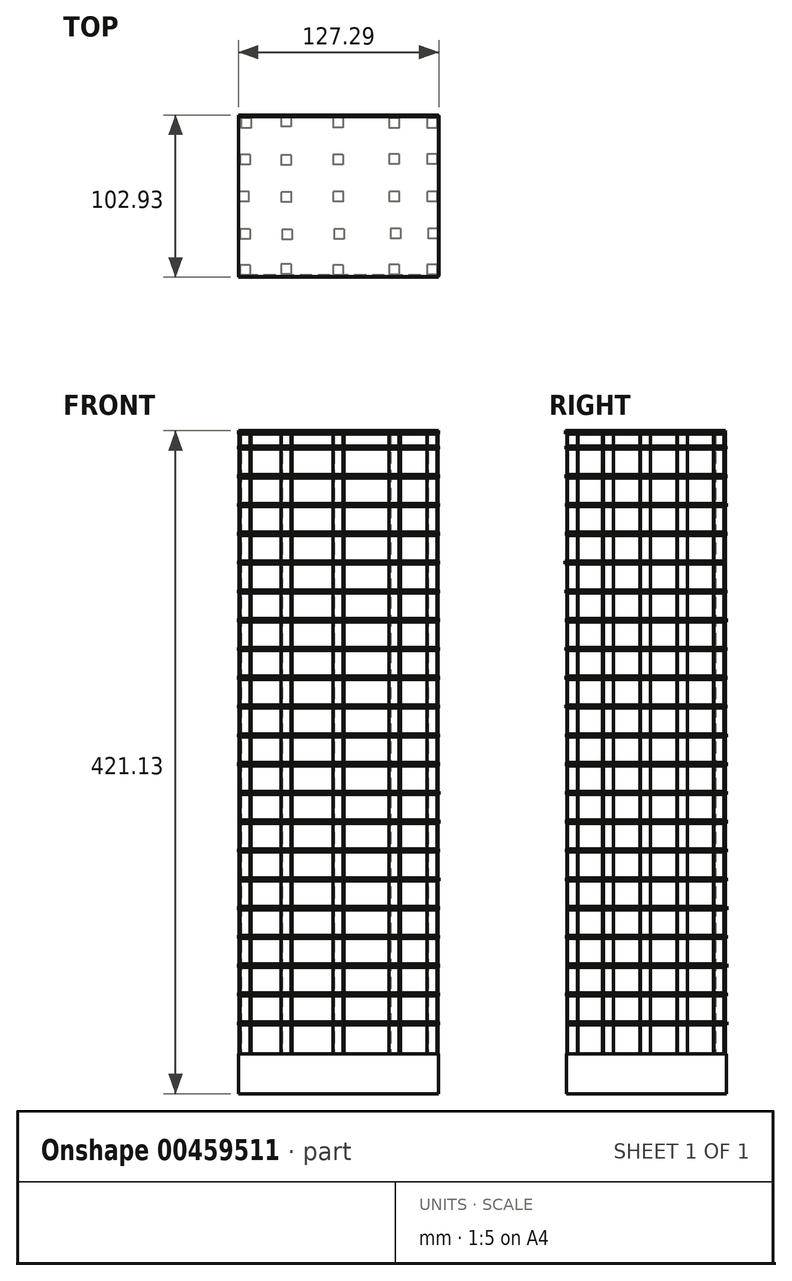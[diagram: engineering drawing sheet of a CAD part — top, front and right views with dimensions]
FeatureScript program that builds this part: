
annotation { "Feature Type Name" : "Feature", "Feature Type Description" : "" }
export const myFeature = defineFeature(function(context is Context, id is Id, definition is map)
    precondition{}
    {
        {
            var Q0;
            Q0=qCreatedBy(makeId("Top.planeOp"),FACE);
            var sketch = newSketch(context, id + "F0", { "sketchPlane" : qUnion([Q0])});
            skLineSegment(sketch, "E0.bottom", {"start": v(63.5, -50.8) * mm, "end": v(-63.5, -50.8) * mm});
            skLineSegment(sketch, "E0.top", {"start": v(63.5, 50.8) * mm, "end": v(-63.5, 50.8) * mm});
            skLineSegment(sketch, "E0.left", {"start": v(63.5, -50.8) * mm, "end": v(63.5, 50.8) * mm});
            skLineSegment(sketch, "E0.right", {"start": v(-63.5, -50.8) * mm, "end": v(-63.5, 50.8) * mm});
            skPoint(sketch, "E0.middle", {"position": v(0, 0) * mm});
            skSolve(sketch);
        }
        {
            var Q0;
            Q0 = qSketchRegion(id + "F0", true);
            extrude(context, id + "F1", {"entities" : qUnion([Q0]), "depth" : 2.03 * mm});
        }
        {
            var Q0;
            Q0=qCreatedBy(makeId("Top.planeOp"),FACE);
            var sketch = newSketch(context, id + "F2", { "sketchPlane" : qUnion([Q0])});
            skLineSegment(sketch, "E1.bottom", {"start": v(63.5, -51.15) * mm, "end": v(-63.5, -51.15) * mm});
            skLineSegment(sketch, "E1.top", {"start": v(63.5, 50.45) * mm, "end": v(-63.5, 50.45) * mm});
            skLineSegment(sketch, "E1.left", {"start": v(63.5, -51.15) * mm, "end": v(63.5, 50.45) * mm});
            skLineSegment(sketch, "E1.right", {"start": v(-63.5, -51.15) * mm, "end": v(-63.5, 50.45) * mm});
            skPoint(sketch, "E1.middle", {"position": v(0, -0.35) * mm});
            skSolve(sketch);
        }
        {
            var Q0;
            Q0=makeQuery(id+"F1.opExtrude","SWEPT_BODY",BODY,{"disambiguationData":[OSD([sQuery(id+"F0.wireOp",EDGE,"E0.bottom"),sQuery(id+"F0.wireOp",EDGE,"E0.top"),sQuery(id+"F0.wireOp",EDGE,"E0.left"),sQuery(id+"F0.wireOp",EDGE,"E0.right")])]});
            transform(context, id + "F3", {"entities" : qUnion([Q0]), "transformType" : TransformType.TRANSLATION_3D, "dx" : 0 * mm, "dy" : 0 * mm, "dz" : 18.29 * mm, "makeCopy" : false});
        }
        {
            var Q0;
            Q0 = qSketchRegion(id + "F2", true);
            extrude(context, id + "F4", {"entities" : qUnion([Q0]), "depth" : 2.03 * mm});
        }
        {
            var Q0;
            Q0=qCreatedBy(makeId("Top.planeOp"),FACE);
            var sketch = newSketch(context, id + "F5", { "sketchPlane" : qUnion([Q0])});
            skLineSegment(sketch, "E2.bottom", {"start": v(63.5, -50.92) * mm, "end": v(-63.5, -50.92) * mm});
            skLineSegment(sketch, "E2.top", {"start": v(63.5, 50.68) * mm, "end": v(-63.5, 50.68) * mm});
            skLineSegment(sketch, "E2.left", {"start": v(63.5, -50.92) * mm, "end": v(63.5, 50.68) * mm});
            skLineSegment(sketch, "E2.right", {"start": v(-63.5, -50.92) * mm, "end": v(-63.5, 50.68) * mm});
            skPoint(sketch, "E2.middle", {"position": v(0, -0.12) * mm});
            skSolve(sketch);
        }
        {
            var Q0;
            Q0=makeQuery(id+"F4.opExtrude","SWEPT_BODY",BODY,{"disambiguationData":[OSD([sQuery(id+"F2.wireOp",EDGE,"E1.bottom"),sQuery(id+"F2.wireOp",EDGE,"E1.top"),sQuery(id+"F2.wireOp",EDGE,"E1.left"),sQuery(id+"F2.wireOp",EDGE,"E1.right")])]});
            transform(context, id + "F6", {"entities" : qUnion([Q0]), "transformType" : TransformType.TRANSLATION_3D, "dx" : 0 * mm, "dy" : 0 * mm, "dz" : 36.58 * mm, "makeCopy" : false});
        }
        {
            var Q0;
            Q0 = qSketchRegion(id + "F5", true);
            extrude(context, id + "F7", {"entities" : qUnion([Q0]), "depth" : 2.03 * mm});
        }
        {
            var Q0;
            Q0=qCreatedBy(makeId("Top.planeOp"),FACE);
            var sketch = newSketch(context, id + "F8", { "sketchPlane" : qUnion([Q0])});
            skLineSegment(sketch, "E3.bottom", {"start": v(63.5, -51.15) * mm, "end": v(-63.5, -51.15) * mm});
            skLineSegment(sketch, "E3.top", {"start": v(63.5, 50.45) * mm, "end": v(-63.5, 50.45) * mm});
            skLineSegment(sketch, "E3.left", {"start": v(63.5, -51.15) * mm, "end": v(63.5, 50.45) * mm});
            skLineSegment(sketch, "E3.right", {"start": v(-63.5, -51.15) * mm, "end": v(-63.5, 50.45) * mm});
            skPoint(sketch, "E3.middle", {"position": v(0, -0.35) * mm});
            skSolve(sketch);
        }
        {
            var Q0;
            Q0=makeQuery(id+"F7.opExtrude","SWEPT_BODY",BODY,{"disambiguationData":[OSD([sQuery(id+"F5.wireOp",EDGE,"E2.bottom"),sQuery(id+"F5.wireOp",EDGE,"E2.top"),sQuery(id+"F5.wireOp",EDGE,"E2.left"),sQuery(id+"F5.wireOp",EDGE,"E2.right")])]});
            transform(context, id + "F9", {"entities" : qUnion([Q0]), "transformType" : TransformType.TRANSLATION_3D, "dx" : 0 * mm, "dy" : 0 * mm, "dz" : 54.86 * mm, "makeCopy" : false});
        }
        {
            var Q0;
            Q0 = qSketchRegion(id + "F8", true);
            var Q1;
            Q1=qNothing();
            extrude(context, id + "F10", {"entities" : qUnion([Q0, Q1]), "operationType" : NewBodyOperationType.ADD, "depth" : 2.03 * mm});
        }
        {
            var Q0;
            Q0=qCreatedBy(makeId("Top.planeOp"),FACE);
            var sketch = newSketch(context, id + "F11", { "sketchPlane" : qUnion([Q0])});
            skLineSegment(sketch, "E4.bottom", {"start": v(63.5, -50.92) * mm, "end": v(-63.5, -50.92) * mm});
            skLineSegment(sketch, "E4.top", {"start": v(63.5, 50.68) * mm, "end": v(-63.5, 50.68) * mm});
            skLineSegment(sketch, "E4.left", {"start": v(63.5, -50.92) * mm, "end": v(63.5, 50.68) * mm});
            skLineSegment(sketch, "E4.right", {"start": v(-63.5, -50.92) * mm, "end": v(-63.5, 50.68) * mm});
            skPoint(sketch, "E4.middle", {"position": v(0, -0.12) * mm});
            skSolve(sketch);
        }
        {
            var Q0;
            Q0=makeQuery(id+"F10.opExtrude","SWEPT_BODY",BODY,{"disambiguationData":[OSD([sQuery(id+"F8.wireOp",EDGE,"E3.bottom"),sQuery(id+"F8.wireOp",EDGE,"E3.top"),sQuery(id+"F8.wireOp",EDGE,"E3.left"),sQuery(id+"F8.wireOp",EDGE,"E3.right")])]});
            transform(context, id + "F12", {"entities" : qUnion([Q0]), "transformType" : TransformType.TRANSLATION_3D, "dx" : 0 * mm, "dy" : 0 * mm, "dz" : 73.15 * mm, "makeCopy" : false});
        }
        {
            var Q0;
            Q0 = qSketchRegion(id + "F11", true);
            extrude(context, id + "F13", {"entities" : qUnion([Q0]), "depth" : 2.03 * mm});
        }
        {
            var Q0;
            Q0=qCreatedBy(makeId("Top.planeOp"),FACE);
            var sketch = newSketch(context, id + "F14", { "sketchPlane" : qUnion([Q0])});
            skLineSegment(sketch, "E5.bottom", {"start": v(63.75, -51.12) * mm, "end": v(-63.25, -51.12) * mm});
            skLineSegment(sketch, "E5.top", {"start": v(63.75, 50.48) * mm, "end": v(-63.25, 50.48) * mm});
            skLineSegment(sketch, "E5.left", {"start": v(63.75, -51.12) * mm, "end": v(63.75, 50.48) * mm});
            skLineSegment(sketch, "E5.right", {"start": v(-63.25, -51.12) * mm, "end": v(-63.25, 50.48) * mm});
            skPoint(sketch, "E5.middle", {"position": v(0.25, -0.32) * mm});
            skSolve(sketch);
        }
        {
            var Q0;
            Q0=makeQuery(id+"F13.opExtrude","SWEPT_BODY",BODY,{"disambiguationData":[OSD([sQuery(id+"F11.wireOp",EDGE,"E4.bottom"),sQuery(id+"F11.wireOp",EDGE,"E4.top"),sQuery(id+"F11.wireOp",EDGE,"E4.left"),sQuery(id+"F11.wireOp",EDGE,"E4.right")])]});
            transform(context, id + "F15", {"entities" : qUnion([Q0]), "transformType" : TransformType.TRANSLATION_3D, "dx" : 0 * mm, "dy" : 0 * mm, "dz" : 91.44 * mm, "makeCopy" : false});
        }
        {
            var Q0;
            Q0 = qSketchRegion(id + "F14", true);
            extrude(context, id + "F16", {"entities" : qUnion([Q0]), "depth" : 2.03 * mm});
        }
        {
            var Q0;
            Q0=qCreatedBy(makeId("Top.planeOp"),FACE);
            var sketch = newSketch(context, id + "F17", { "sketchPlane" : qUnion([Q0])});
            skLineSegment(sketch, "E6.bottom", {"start": v(63.56, -50.99) * mm, "end": v(-63.44, -50.99) * mm});
            skLineSegment(sketch, "E6.top", {"start": v(63.56, 50.61) * mm, "end": v(-63.44, 50.61) * mm});
            skLineSegment(sketch, "E6.left", {"start": v(63.56, -50.99) * mm, "end": v(63.56, 50.61) * mm});
            skLineSegment(sketch, "E6.right", {"start": v(-63.44, -50.99) * mm, "end": v(-63.44, 50.61) * mm});
            skPoint(sketch, "E6.middle", {"position": v(0.06, -0.19) * mm});
            skSolve(sketch);
        }
        {
            var Q0;
            Q0=makeQuery(id+"F16.opExtrude","SWEPT_BODY",BODY,{"disambiguationData":[OSD([sQuery(id+"F14.wireOp",EDGE,"E5.bottom"),sQuery(id+"F14.wireOp",EDGE,"E5.top"),sQuery(id+"F14.wireOp",EDGE,"E5.left"),sQuery(id+"F14.wireOp",EDGE,"E5.right")])]});
            transform(context, id + "F18", {"entities" : qUnion([Q0]), "transformType" : TransformType.TRANSLATION_3D, "dx" : 0 * mm, "dy" : 0 * mm, "dz" : 109.73 * mm, "makeCopy" : false});
        }
        {
            var Q0;
            Q0 = qSketchRegion(id + "F17", true);
            extrude(context, id + "F19", {"entities" : qUnion([Q0]), "depth" : 2.03 * mm});
        }
        {
            var Q0;
            Q0=qCreatedBy(makeId("Top.planeOp"),FACE);
            var sketch = newSketch(context, id + "F20", { "sketchPlane" : qUnion([Q0])});
            skLineSegment(sketch, "E7.bottom", {"start": v(63.79, -51.09) * mm, "end": v(-63.21, -51.09) * mm});
            skLineSegment(sketch, "E7.top", {"start": v(63.79, 50.51) * mm, "end": v(-63.21, 50.51) * mm});
            skLineSegment(sketch, "E7.left", {"start": v(63.79, -51.09) * mm, "end": v(63.79, 50.51) * mm});
            skLineSegment(sketch, "E7.right", {"start": v(-63.21, -51.09) * mm, "end": v(-63.21, 50.51) * mm});
            skSolve(sketch);
        }
        {
            var Q0;
            Q0=makeQuery(id+"F19.opExtrude","SWEPT_BODY",BODY,{"disambiguationData":[OSD([sQuery(id+"F17.wireOp",EDGE,"E6.bottom"),sQuery(id+"F17.wireOp",EDGE,"E6.top"),sQuery(id+"F17.wireOp",EDGE,"E6.left"),sQuery(id+"F17.wireOp",EDGE,"E6.right")])]});
            transform(context, id + "F21", {"entities" : qUnion([Q0]), "transformType" : TransformType.TRANSLATION_3D, "dx" : 0 * mm, "dy" : 0 * mm, "dz" : 128.02 * mm, "makeCopy" : false});
        }
        {
            var Q0;
            Q0 = qSketchRegion(id + "F20", true);
            extrude(context, id + "F22", {"entities" : qUnion([Q0]), "depth" : 2.03 * mm});
        }
        {
            var Q0;
            Q0=qCreatedBy(makeId("Top.planeOp"),FACE);
            var sketch = newSketch(context, id + "F23", { "sketchPlane" : qUnion([Q0])});
            skLineSegment(sketch, "E8.bottom", {"start": v(63.79, -51.09) * mm, "end": v(-63.21, -51.09) * mm});
            skLineSegment(sketch, "E8.top", {"start": v(63.79, 50.51) * mm, "end": v(-63.21, 50.51) * mm});
            skLineSegment(sketch, "E8.left", {"start": v(63.79, -51.09) * mm, "end": v(63.79, 50.51) * mm});
            skLineSegment(sketch, "E8.right", {"start": v(-63.21, -51.09) * mm, "end": v(-63.21, 50.51) * mm});
            skSolve(sketch);
        }
        {
            var Q0;
            Q0=makeQuery(id+"F22.opExtrude","SWEPT_BODY",BODY,{"disambiguationData":[OSD([sQuery(id+"F20.wireOp",EDGE,"E7.bottom"),sQuery(id+"F20.wireOp",EDGE,"E7.top"),sQuery(id+"F20.wireOp",EDGE,"E7.left"),sQuery(id+"F20.wireOp",EDGE,"E7.right")])]});
            transform(context, id + "F24", {"entities" : qUnion([Q0]), "transformType" : TransformType.TRANSLATION_3D, "dx" : 0 * mm, "dy" : 0 * mm, "dz" : 146.3 * mm, "makeCopy" : false});
        }
        {
            var Q0;
            Q0 = qSketchRegion(id + "F23", true);
            extrude(context, id + "F25", {"entities" : qUnion([Q0]), "depth" : 2.03 * mm});
        }
        {
            var Q0;
            Q0=qCreatedBy(makeId("Top.planeOp"),FACE);
            var sketch = newSketch(context, id + "F26", { "sketchPlane" : qUnion([Q0])});
            skLineSegment(sketch, "E9.bottom", {"start": v(63.5, -51.09) * mm, "end": v(-63.5, -51.09) * mm});
            skLineSegment(sketch, "E9.top", {"start": v(63.5, 50.51) * mm, "end": v(-63.5, 50.51) * mm});
            skLineSegment(sketch, "E9.left", {"start": v(63.5, -51.09) * mm, "end": v(63.5, 50.51) * mm});
            skLineSegment(sketch, "E9.right", {"start": v(-63.5, -51.09) * mm, "end": v(-63.5, 50.51) * mm});
            skSolve(sketch);
        }
        {
            var Q0;
            Q0=makeQuery(id+"F25.opExtrude","SWEPT_BODY",BODY,{"disambiguationData":[OSD([sQuery(id+"F23.wireOp",EDGE,"E8.bottom"),sQuery(id+"F23.wireOp",EDGE,"E8.top"),sQuery(id+"F23.wireOp",EDGE,"E8.left"),sQuery(id+"F23.wireOp",EDGE,"E8.right")])]});
            transform(context, id + "F27", {"entities" : qUnion([Q0]), "transformType" : TransformType.TRANSLATION_3D, "dx" : 0 * mm, "dy" : 0 * mm, "dz" : 164.6 * mm, "makeCopy" : false});
        }
        {
            var Q0;
            Q0 = qSketchRegion(id + "F26", true);
            extrude(context, id + "F28", {"entities" : qUnion([Q0]), "depth" : 2.03 * mm});
        }
        {
            var Q0;
            Q0=qCreatedBy(makeId("Top.planeOp"),FACE);
            var sketch = newSketch(context, id + "F29", { "sketchPlane" : qUnion([Q0])});
            skLineSegment(sketch, "E10.bottom", {"start": v(63.5, -51.09) * mm, "end": v(-63.5, -51.09) * mm});
            skLineSegment(sketch, "E10.top", {"start": v(63.5, 50.51) * mm, "end": v(-63.5, 50.51) * mm});
            skLineSegment(sketch, "E10.left", {"start": v(63.5, -51.09) * mm, "end": v(63.5, 50.51) * mm});
            skLineSegment(sketch, "E10.right", {"start": v(-63.5, -51.09) * mm, "end": v(-63.5, 50.51) * mm});
            skSolve(sketch);
        }
        {
            var Q0;
            Q0=makeQuery(id+"F28.opExtrude","SWEPT_BODY",BODY,{"disambiguationData":[OSD([sQuery(id+"F26.wireOp",EDGE,"E9.bottom"),sQuery(id+"F26.wireOp",EDGE,"E9.top"),sQuery(id+"F26.wireOp",EDGE,"E9.left"),sQuery(id+"F26.wireOp",EDGE,"E9.right")])]});
            transform(context, id + "F30", {"entities" : qUnion([Q0]), "transformType" : TransformType.TRANSLATION_3D, "dx" : 0 * mm, "dy" : 0 * mm, "dz" : 182.88 * mm, "makeCopy" : false});
        }
        {
            var Q0;
            Q0 = qSketchRegion(id + "F29", true);
            extrude(context, id + "F31", {"entities" : qUnion([Q0]), "depth" : 2.03 * mm});
        }
        {
            var Q0;
            Q0=qCreatedBy(makeId("Top.planeOp"),FACE);
            var sketch = newSketch(context, id + "F32", { "sketchPlane" : qUnion([Q0])});
            skLineSegment(sketch, "E11.bottom", {"start": v(63.5, -51.35) * mm, "end": v(-63.5, -51.35) * mm});
            skLineSegment(sketch, "E11.top", {"start": v(63.5, 50.25) * mm, "end": v(-63.5, 50.25) * mm});
            skLineSegment(sketch, "E11.left", {"start": v(63.5, -51.35) * mm, "end": v(63.5, 50.25) * mm});
            skLineSegment(sketch, "E11.right", {"start": v(-63.5, -51.35) * mm, "end": v(-63.5, 50.25) * mm});
            skSolve(sketch);
        }
        {
            var Q0;
            Q0=makeQuery(id+"F31.opExtrude","SWEPT_BODY",BODY,{"disambiguationData":[OSD([sQuery(id+"F29.wireOp",EDGE,"E10.bottom"),sQuery(id+"F29.wireOp",EDGE,"E10.top"),sQuery(id+"F29.wireOp",EDGE,"E10.left"),sQuery(id+"F29.wireOp",EDGE,"E10.right")])]});
            transform(context, id + "F33", {"entities" : qUnion([Q0]), "transformType" : TransformType.TRANSLATION_3D, "dx" : 0 * mm, "dy" : 0 * mm, "dz" : 201.17 * mm, "makeCopy" : false});
        }
        {
            var Q0;
            Q0 = qSketchRegion(id + "F32", true);
            extrude(context, id + "F34", {"entities" : qUnion([Q0]), "depth" : 2.03 * mm});
        }
        {
            var Q0;
            Q0=qCreatedBy(makeId("Top.planeOp"),FACE);
            var sketch = newSketch(context, id + "F35", { "sketchPlane" : qUnion([Q0])});
            skLineSegment(sketch, "E12.bottom", {"start": v(63.5, -51.42) * mm, "end": v(-63.5, -51.42) * mm});
            skLineSegment(sketch, "E12.top", {"start": v(63.5, 50.18) * mm, "end": v(-63.5, 50.18) * mm});
            skLineSegment(sketch, "E12.left", {"start": v(63.5, -51.42) * mm, "end": v(63.5, 50.18) * mm});
            skLineSegment(sketch, "E12.right", {"start": v(-63.5, -51.42) * mm, "end": v(-63.5, 50.18) * mm});
            skSolve(sketch);
        }
        {
            var Q0;
            Q0=makeQuery(id+"F34.opExtrude","SWEPT_BODY",BODY,{"disambiguationData":[OSD([sQuery(id+"F32.wireOp",EDGE,"E11.bottom"),sQuery(id+"F32.wireOp",EDGE,"E11.top"),sQuery(id+"F32.wireOp",EDGE,"E11.left"),sQuery(id+"F32.wireOp",EDGE,"E11.right")])]});
            transform(context, id + "F36", {"entities" : qUnion([Q0]), "transformType" : TransformType.TRANSLATION_3D, "dx" : 0 * mm, "dy" : 0 * mm, "dz" : 219.46 * mm, "makeCopy" : false});
        }
        {
            var Q0;
            Q0=makeQuery(id+"F35.imprint","IMPRINT",FACE,{"disambiguationData":[TD([[makeQuery(id+"F35.imprint","IMPRINT",EDGE,{"derivedFrom":sQuery(id+"F35.wireOp",EDGE,"E12.bottom")}),-1.0]])]});
            extrude(context, id + "F37", {"entities" : qUnion([Q0]), "depth" : 2.03 * mm});
        }
        {
            var Q0;
            Q0=qCreatedBy(makeId("Top.planeOp"),FACE);
            var sketch = newSketch(context, id + "F38", { "sketchPlane" : qUnion([Q0])});
            skLineSegment(sketch, "E13.bottom", {"start": v(63.5, -51.4) * mm, "end": v(-63.5, -51.4) * mm});
            skLineSegment(sketch, "E13.top", {"start": v(63.5, 50.2) * mm, "end": v(-63.5, 50.2) * mm});
            skLineSegment(sketch, "E13.left", {"start": v(63.5, -51.4) * mm, "end": v(63.5, 50.2) * mm});
            skLineSegment(sketch, "E13.right", {"start": v(-63.5, -51.4) * mm, "end": v(-63.5, 50.2) * mm});
            skSolve(sketch);
        }
        {
            var Q0;
            Q0=makeQuery(id+"F37.opExtrude","SWEPT_BODY",BODY,{"disambiguationData":[OSD([sQuery(id+"F35.wireOp",EDGE,"E12.bottom"),sQuery(id+"F35.wireOp",EDGE,"E12.top"),sQuery(id+"F35.wireOp",EDGE,"E12.left"),sQuery(id+"F35.wireOp",EDGE,"E12.right")])]});
            transform(context, id + "F39", {"entities" : qUnion([Q0]), "transformType" : TransformType.TRANSLATION_3D, "dx" : 0 * mm, "dy" : 0 * mm, "dz" : 237.74 * mm, "makeCopy" : false});
        }
        {
            var Q0;
            Q0=makeQuery(id+"F38.imprint","IMPRINT",FACE,{"disambiguationData":[TD([[makeQuery(id+"F38.imprint","IMPRINT",EDGE,{"derivedFrom":sQuery(id+"F38.wireOp",EDGE,"E13.bottom")}),-1.0]])]});
            extrude(context, id + "F40", {"entities" : qUnion([Q0]), "depth" : 2.03 * mm});
        }
        {
            var Q0;
            Q0=qCreatedBy(makeId("Top.planeOp"),FACE);
            var sketch = newSketch(context, id + "F41", { "sketchPlane" : qUnion([Q0])});
            skLineSegment(sketch, "E14.bottom", {"start": v(63.5, -51.26) * mm, "end": v(-63.5, -51.26) * mm});
            skLineSegment(sketch, "E14.top", {"start": v(63.5, 50.34) * mm, "end": v(-63.5, 50.34) * mm});
            skLineSegment(sketch, "E14.left", {"start": v(63.5, -51.26) * mm, "end": v(63.5, 50.34) * mm});
            skLineSegment(sketch, "E14.right", {"start": v(-63.5, -51.26) * mm, "end": v(-63.5, 50.34) * mm});
            skSolve(sketch);
        }
        {
            var Q0;
            Q0=makeQuery(id+"F40.opExtrude","SWEPT_BODY",BODY,{"disambiguationData":[OSD([sQuery(id+"F38.wireOp",EDGE,"E13.bottom"),sQuery(id+"F38.wireOp",EDGE,"E13.top"),sQuery(id+"F38.wireOp",EDGE,"E13.left"),sQuery(id+"F38.wireOp",EDGE,"E13.right")])]});
            transform(context, id + "F42", {"entities" : qUnion([Q0]), "transformType" : TransformType.TRANSLATION_3D, "dx" : 0 * mm, "dy" : 0 * mm, "dz" : 256.03 * mm, "makeCopy" : false});
        }
        {
            var Q0;
            Q0=makeQuery(id+"F41.imprint","IMPRINT",FACE,{"disambiguationData":[TD([[makeQuery(id+"F41.imprint","IMPRINT",EDGE,{"derivedFrom":sQuery(id+"F41.wireOp",EDGE,"E14.bottom")}),-1.0]])]});
            extrude(context, id + "F43", {"entities" : qUnion([Q0]), "depth" : 2.03 * mm});
        }
        {
            var Q0;
            Q0=qCreatedBy(makeId("Top.planeOp"),FACE);
            var sketch = newSketch(context, id + "F44", { "sketchPlane" : qUnion([Q0])});
            skLineSegment(sketch, "E15.bottom", {"start": v(63.5, -51.43) * mm, "end": v(-63.5, -51.43) * mm});
            skLineSegment(sketch, "E15.top", {"start": v(63.5, 50.17) * mm, "end": v(-63.5, 50.17) * mm});
            skLineSegment(sketch, "E15.left", {"start": v(63.5, -51.43) * mm, "end": v(63.5, 50.17) * mm});
            skLineSegment(sketch, "E15.right", {"start": v(-63.5, -51.43) * mm, "end": v(-63.5, 50.17) * mm});
            skSolve(sketch);
        }
        {
            var Q0;
            Q0=makeQuery(id+"F43.opExtrude","SWEPT_BODY",BODY,{"disambiguationData":[OSD([sQuery(id+"F41.wireOp",EDGE,"E14.bottom"),sQuery(id+"F41.wireOp",EDGE,"E14.top"),sQuery(id+"F41.wireOp",EDGE,"E14.left"),sQuery(id+"F41.wireOp",EDGE,"E14.right")])]});
            transform(context, id + "F45", {"entities" : qUnion([Q0]), "transformType" : TransformType.TRANSLATION_3D, "dx" : 0 * mm, "dy" : 0 * mm, "dz" : 274.32 * mm, "makeCopy" : false});
        }
        {
            var Q0;
            Q0=makeQuery(id+"F44.imprint","IMPRINT",FACE,{"disambiguationData":[TD([[makeQuery(id+"F44.imprint","IMPRINT",EDGE,{"derivedFrom":sQuery(id+"F44.wireOp",EDGE,"E15.bottom")}),-1.0]])]});
            extrude(context, id + "F46", {"entities" : qUnion([Q0]), "depth" : 2.03 * mm});
        }
        {
            var Q0;
            Q0=qCreatedBy(makeId("Top.planeOp"),FACE);
            var sketch = newSketch(context, id + "F47", { "sketchPlane" : qUnion([Q0])});
            skLineSegment(sketch, "E16.bottom", {"start": v(63.5, -52.13) * mm, "end": v(-63.5, -52.13) * mm});
            skLineSegment(sketch, "E16.top", {"start": v(63.5, 49.47) * mm, "end": v(-63.5, 49.47) * mm});
            skLineSegment(sketch, "E16.left", {"start": v(63.5, -52.13) * mm, "end": v(63.5, 49.47) * mm});
            skLineSegment(sketch, "E16.right", {"start": v(-63.5, -52.13) * mm, "end": v(-63.5, 49.47) * mm});
            skSolve(sketch);
        }
        {
            var Q0;
            Q0=makeQuery(id+"F46.opExtrude","SWEPT_BODY",BODY,{"disambiguationData":[OSD([sQuery(id+"F44.wireOp",EDGE,"E15.bottom"),sQuery(id+"F44.wireOp",EDGE,"E15.top"),sQuery(id+"F44.wireOp",EDGE,"E15.left"),sQuery(id+"F44.wireOp",EDGE,"E15.right")])]});
            transform(context, id + "F48", {"entities" : qUnion([Q0]), "transformType" : TransformType.TRANSLATION_3D, "dx" : 0 * mm, "dy" : 0 * mm, "dz" : 292.6 * mm, "makeCopy" : false});
        }
        {
            var Q0;
            Q0=makeQuery(id+"F47.imprint","IMPRINT",FACE,{"disambiguationData":[TD([[makeQuery(id+"F47.imprint","IMPRINT",EDGE,{"derivedFrom":sQuery(id+"F47.wireOp",EDGE,"E16.bottom")}),-1.0]])]});
            extrude(context, id + "F49", {"entities" : qUnion([Q0]), "depth" : 2.03 * mm});
        }
        {
            var Q0;
            Q0=qCreatedBy(makeId("Top.planeOp"),FACE);
            var sketch = newSketch(context, id + "F50", { "sketchPlane" : qUnion([Q0])});
            skLineSegment(sketch, "E17.bottom", {"start": v(63.5, -51.27) * mm, "end": v(-63.5, -51.27) * mm});
            skLineSegment(sketch, "E17.top", {"start": v(63.5, 50.33) * mm, "end": v(-63.5, 50.33) * mm});
            skLineSegment(sketch, "E17.left", {"start": v(63.5, -51.27) * mm, "end": v(63.5, 50.33) * mm});
            skLineSegment(sketch, "E17.right", {"start": v(-63.5, -51.27) * mm, "end": v(-63.5, 50.33) * mm});
            skSolve(sketch);
        }
        {
            var Q0;
            Q0=makeQuery(id+"F49.opExtrude","SWEPT_BODY",BODY,{"disambiguationData":[OSD([sQuery(id+"F47.wireOp",EDGE,"E16.bottom"),sQuery(id+"F47.wireOp",EDGE,"E16.top"),sQuery(id+"F47.wireOp",EDGE,"E16.left"),sQuery(id+"F47.wireOp",EDGE,"E16.right")])]});
            transform(context, id + "F51", {"entities" : qUnion([Q0]), "transformType" : TransformType.TRANSLATION_3D, "dx" : 0 * mm, "dy" : 0 * mm, "dz" : 310.9 * mm, "makeCopy" : false});
        }
        {
            var Q0;
            Q0=makeQuery(id+"F50.imprint","IMPRINT",FACE,{"disambiguationData":[TD([[makeQuery(id+"F50.imprint","IMPRINT",EDGE,{"derivedFrom":sQuery(id+"F50.wireOp",EDGE,"E17.bottom")}),-1.0]])]});
            extrude(context, id + "F52", {"entities" : qUnion([Q0]), "depth" : 2.03 * mm});
        }
        {
            var Q0;
            Q0=qCreatedBy(makeId("Top.planeOp"),FACE);
            var sketch = newSketch(context, id + "F53", { "sketchPlane" : qUnion([Q0])});
            skLineSegment(sketch, "E18.bottom", {"start": v(63.5, -51.08) * mm, "end": v(-63.5, -51.08) * mm});
            skLineSegment(sketch, "E18.top", {"start": v(63.5, 50.52) * mm, "end": v(-63.5, 50.52) * mm});
            skLineSegment(sketch, "E18.left", {"start": v(63.5, -51.08) * mm, "end": v(63.5, 50.52) * mm});
            skLineSegment(sketch, "E18.right", {"start": v(-63.5, -51.08) * mm, "end": v(-63.5, 50.52) * mm});
            skSolve(sketch);
        }
        {
            var Q0;
            Q0=makeQuery(id+"F52.opExtrude","SWEPT_BODY",BODY,{"disambiguationData":[OSD([sQuery(id+"F50.wireOp",EDGE,"E17.bottom"),sQuery(id+"F50.wireOp",EDGE,"E17.top"),sQuery(id+"F50.wireOp",EDGE,"E17.left"),sQuery(id+"F50.wireOp",EDGE,"E17.right")])]});
            transform(context, id + "F54", {"entities" : qUnion([Q0]), "transformType" : TransformType.TRANSLATION_3D, "dx" : 0 * mm, "dy" : 0 * mm, "dz" : 329.18 * mm, "makeCopy" : false});
        }
        {
            var Q0;
            Q0=makeQuery(id+"F53.imprint","IMPRINT",FACE,{"disambiguationData":[TD([[makeQuery(id+"F53.imprint","IMPRINT",EDGE,{"derivedFrom":sQuery(id+"F53.wireOp",EDGE,"E18.bottom")}),-1.0]])]});
            extrude(context, id + "F55", {"entities" : qUnion([Q0]), "depth" : 2.03 * mm});
        }
        {
            var Q0;
            Q0=qCreatedBy(makeId("Top.planeOp"),FACE);
            var sketch = newSketch(context, id + "F56", { "sketchPlane" : qUnion([Q0])});
            skLineSegment(sketch, "E19.bottom", {"start": v(63.5, -51.56) * mm, "end": v(-63.5, -51.56) * mm});
            skLineSegment(sketch, "E19.top", {"start": v(63.5, 50.04) * mm, "end": v(-63.5, 50.04) * mm});
            skLineSegment(sketch, "E19.left", {"start": v(63.5, -51.56) * mm, "end": v(63.5, 50.04) * mm});
            skLineSegment(sketch, "E19.right", {"start": v(-63.5, -51.56) * mm, "end": v(-63.5, 50.04) * mm});
            skSolve(sketch);
        }
        {
            var Q0;
            Q0=makeQuery(id+"F55.opExtrude","SWEPT_BODY",BODY,{"disambiguationData":[OSD([sQuery(id+"F53.wireOp",EDGE,"E18.bottom"),sQuery(id+"F53.wireOp",EDGE,"E18.top"),sQuery(id+"F53.wireOp",EDGE,"E18.left"),sQuery(id+"F53.wireOp",EDGE,"E18.right")])]});
            transform(context, id + "F57", {"entities" : qUnion([Q0]), "transformType" : TransformType.TRANSLATION_3D, "dx" : 0 * mm, "dy" : 0 * mm, "dz" : 347.47 * mm, "makeCopy" : false});
        }
        {
            var Q0;
            Q0=makeQuery(id+"F56.imprint","IMPRINT",FACE,{"disambiguationData":[TD([[makeQuery(id+"F56.imprint","IMPRINT",EDGE,{"derivedFrom":sQuery(id+"F56.wireOp",EDGE,"E19.bottom")}),-1.0]])]});
            extrude(context, id + "F58", {"entities" : qUnion([Q0]), "depth" : 2.03 * mm});
        }
        {
            var Q0;
            Q0=qCreatedBy(makeId("Top.planeOp"),FACE);
            var sketch = newSketch(context, id + "F59", { "sketchPlane" : qUnion([Q0])});
            skLineSegment(sketch, "E20.bottom", {"start": v(63.5, -51.36) * mm, "end": v(-63.5, -51.36) * mm});
            skLineSegment(sketch, "E20.top", {"start": v(63.5, 50.24) * mm, "end": v(-63.5, 50.24) * mm});
            skLineSegment(sketch, "E20.left", {"start": v(63.5, -51.36) * mm, "end": v(63.5, 50.24) * mm});
            skLineSegment(sketch, "E20.right", {"start": v(-63.5, -51.36) * mm, "end": v(-63.5, 50.24) * mm});
            skSolve(sketch);
        }
        {
            var Q0;
            Q0=makeQuery(id+"F58.opExtrude","SWEPT_BODY",BODY,{"disambiguationData":[OSD([sQuery(id+"F56.wireOp",EDGE,"E19.bottom"),sQuery(id+"F56.wireOp",EDGE,"E19.top"),sQuery(id+"F56.wireOp",EDGE,"E19.left"),sQuery(id+"F56.wireOp",EDGE,"E19.right")])]});
            transform(context, id + "F60", {"entities" : qUnion([Q0]), "transformType" : TransformType.TRANSLATION_3D, "dx" : 0 * mm, "dy" : 0 * mm, "dz" : 365.76 * mm, "makeCopy" : false});
        }
        {
            var Q0;
            Q0=makeQuery(id+"F59.imprint","IMPRINT",FACE,{"disambiguationData":[TD([[makeQuery(id+"F59.imprint","IMPRINT",EDGE,{"derivedFrom":sQuery(id+"F59.wireOp",EDGE,"E20.bottom")}),-1.0]])]});
            extrude(context, id + "F61", {"entities" : qUnion([Q0]), "depth" : 2.03 * mm});
        }
        {
            var Q0;
            Q0=qCreatedBy(makeId("Top.planeOp"),FACE);
            var sketch = newSketch(context, id + "F62", { "sketchPlane" : qUnion([Q0])});
            skLineSegment(sketch, "E21.bottom", {"start": v(63.5, -51.64) * mm, "end": v(-63.5, -51.64) * mm});
            skLineSegment(sketch, "E21.top", {"start": v(63.5, 49.96) * mm, "end": v(-63.5, 49.96) * mm});
            skLineSegment(sketch, "E21.left", {"start": v(63.5, -51.64) * mm, "end": v(63.5, 49.96) * mm});
            skLineSegment(sketch, "E21.right", {"start": v(-63.5, -51.64) * mm, "end": v(-63.5, 49.96) * mm});
            skSolve(sketch);
        }
        {
            var Q0;
            Q0=makeQuery(id+"F61.opExtrude","SWEPT_BODY",BODY,{"disambiguationData":[OSD([sQuery(id+"F59.wireOp",EDGE,"E20.bottom"),sQuery(id+"F59.wireOp",EDGE,"E20.top"),sQuery(id+"F59.wireOp",EDGE,"E20.left"),sQuery(id+"F59.wireOp",EDGE,"E20.right")])]});
            transform(context, id + "F63", {"entities" : qUnion([Q0]), "transformType" : TransformType.TRANSLATION_3D, "dx" : 0 * mm, "dy" : 0 * mm, "dz" : 384.05 * mm, "makeCopy" : false});
        }
        {
            var Q0;
            Q0=makeQuery(id+"F62.imprint","IMPRINT",FACE,{"disambiguationData":[TD([[makeQuery(id+"F62.imprint","IMPRINT",EDGE,{"derivedFrom":sQuery(id+"F62.wireOp",EDGE,"E21.bottom")}),-1.0]])]});
            extrude(context, id + "F64", {"entities" : qUnion([Q0]), "depth" : 2.03 * mm});
        }
        {
            var Q0;
            Q0=qCreatedBy(makeId("Top.planeOp"),FACE);
            var sketch = newSketch(context, id + "F65", { "sketchPlane" : qUnion([Q0])});
            skLineSegment(sketch, "E22.bottom", {"start": v(63.5, -51.15) * mm, "end": v(-63.5, -51.15) * mm});
            skLineSegment(sketch, "E22.top", {"start": v(63.5, 50.45) * mm, "end": v(-63.5, 50.45) * mm});
            skLineSegment(sketch, "E22.left", {"start": v(63.5, -51.15) * mm, "end": v(63.5, 50.45) * mm});
            skLineSegment(sketch, "E22.right", {"start": v(-63.5, -51.15) * mm, "end": v(-63.5, 50.45) * mm});
            skSolve(sketch);
        }
        {
            var Q0;
            Q0=makeQuery(id+"F64.opExtrude","SWEPT_BODY",BODY,{"disambiguationData":[OSD([sQuery(id+"F62.wireOp",EDGE,"E21.bottom"),sQuery(id+"F62.wireOp",EDGE,"E21.top"),sQuery(id+"F62.wireOp",EDGE,"E21.left"),sQuery(id+"F62.wireOp",EDGE,"E21.right")])]});
            transform(context, id + "F66", {"entities" : qUnion([Q0]), "transformType" : TransformType.TRANSLATION_3D, "dx" : 0 * mm, "dy" : 0 * mm, "dz" : 393.7 * mm, "makeCopy" : false});
        }
        {
            var Q0;
            Q0=makeQuery(id+"F65.imprint","IMPRINT",FACE,{"disambiguationData":[TD([[makeQuery(id+"F65.imprint","IMPRINT",EDGE,{"derivedFrom":sQuery(id+"F65.wireOp",EDGE,"E22.bottom")}),-1.0]])]});
            extrude(context, id + "F67", {"entities" : qUnion([Q0]), "oppositeDirection" : true, "depth" : 25.4 * mm});
        }
        {
            var Q0;
            Q0=qCreatedBy(makeId("Top.planeOp"),FACE);
            var sketch = newSketch(context, id + "F68", { "sketchPlane" : qUnion([Q0])});
            skLineSegment(sketch, "E23.bottom", {"start": v(3.17, -4.2) * mm, "end": v(-3.18, -4.2) * mm});
            skLineSegment(sketch, "E23.top", {"start": v(3.18, 2.16) * mm, "end": v(-3.17, 2.16) * mm});
            skLineSegment(sketch, "E23.left", {"start": v(3.17, -4.2) * mm, "end": v(3.18, 2.16) * mm});
            skLineSegment(sketch, "E23.right", {"start": v(-3.18, -4.2) * mm, "end": v(-3.18, 2.16) * mm});
            skPoint(sketch, "E23.middle", {"position": v(0, 0) * mm});
            skLineSegment(sketch, "E24.bottom", {"start": v(2.96, 25.78) * mm, "end": v(-3.39, 25.78) * mm});
            skLineSegment(sketch, "E24.top", {"start": v(2.96, 19.43) * mm, "end": v(-3.39, 19.43) * mm});
            skLineSegment(sketch, "E24.left", {"start": v(2.96, 25.78) * mm, "end": v(2.96, 19.43) * mm});
            skLineSegment(sketch, "E24.right", {"start": v(-3.39, 25.78) * mm, "end": v(-3.39, 19.43) * mm});
            skLineSegment(sketch, "E25.bottom", {"start": v(2.96, 49.15) * mm, "end": v(-3.39, 49.15) * mm});
            skLineSegment(sketch, "E25.top", {"start": v(2.96, 42.8) * mm, "end": v(-3.39, 42.8) * mm});
            skLineSegment(sketch, "E25.left", {"start": v(2.96, 49.15) * mm, "end": v(2.96, 42.8) * mm});
            skLineSegment(sketch, "E25.right", {"start": v(-3.39, 49.15) * mm, "end": v(-3.39, 42.8) * mm});
            skLineSegment(sketch, "E26.bottom", {"start": v(3.6, -21.46) * mm, "end": v(-2.75, -21.46) * mm});
            skLineSegment(sketch, "E26.top", {"start": v(3.6, -27.81) * mm, "end": v(-2.75, -27.81) * mm});
            skLineSegment(sketch, "E26.left", {"start": v(3.6, -21.46) * mm, "end": v(3.6, -27.81) * mm});
            skLineSegment(sketch, "E26.right", {"start": v(-2.75, -21.46) * mm, "end": v(-2.75, -27.81) * mm});
            skLineSegment(sketch, "E27.bottom", {"start": v(2.96, -44.32) * mm, "end": v(-3.39, -44.32) * mm});
            skLineSegment(sketch, "E27.top", {"start": v(2.96, -50.67) * mm, "end": v(-3.39, -50.67) * mm});
            skLineSegment(sketch, "E27.left", {"start": v(2.96, -44.32) * mm, "end": v(2.96, -50.67) * mm});
            skLineSegment(sketch, "E27.right", {"start": v(-3.39, -44.32) * mm, "end": v(-3.39, -50.67) * mm});
            skLineSegment(sketch, "E28.bottom", {"start": v(38.8, -4.1) * mm, "end": v(32.45, -4.1) * mm});
            skLineSegment(sketch, "E28.top", {"start": v(38.8, 2.24) * mm, "end": v(32.45, 2.24) * mm});
            skLineSegment(sketch, "E28.left", {"start": v(38.8, -4.1) * mm, "end": v(38.8, 2.24) * mm});
            skLineSegment(sketch, "E28.right", {"start": v(32.45, -4.1) * mm, "end": v(32.45, 2.24) * mm});
            skLineSegment(sketch, "E29.bottom", {"start": v(38.59, 25.87) * mm, "end": v(32.24, 25.87) * mm});
            skLineSegment(sketch, "E29.top", {"start": v(38.59, 19.52) * mm, "end": v(32.24, 19.52) * mm});
            skLineSegment(sketch, "E29.left", {"start": v(38.59, 25.87) * mm, "end": v(38.59, 19.52) * mm});
            skLineSegment(sketch, "E29.right", {"start": v(32.24, 25.87) * mm, "end": v(32.24, 19.52) * mm});
            skLineSegment(sketch, "E30.bottom", {"start": v(38.59, 48.73) * mm, "end": v(32.24, 48.73) * mm});
            skLineSegment(sketch, "E30.top", {"start": v(38.59, 42.38) * mm, "end": v(32.24, 42.38) * mm});
            skLineSegment(sketch, "E30.left", {"start": v(38.59, 48.73) * mm, "end": v(38.59, 42.38) * mm});
            skLineSegment(sketch, "E30.right", {"start": v(32.24, 48.73) * mm, "end": v(32.24, 42.38) * mm});
            skLineSegment(sketch, "E31.bottom", {"start": v(39.23, -21.38) * mm, "end": v(32.88, -21.38) * mm});
            skLineSegment(sketch, "E31.top", {"start": v(39.23, -27.73) * mm, "end": v(32.88, -27.73) * mm});
            skLineSegment(sketch, "E31.left", {"start": v(39.23, -21.38) * mm, "end": v(39.23, -27.73) * mm});
            skLineSegment(sketch, "E31.right", {"start": v(32.88, -21.38) * mm, "end": v(32.88, -27.73) * mm});
            skLineSegment(sketch, "E32.bottom", {"start": v(38.59, -44.24) * mm, "end": v(32.24, -44.24) * mm});
            skLineSegment(sketch, "E32.top", {"start": v(38.59, -50.59) * mm, "end": v(32.24, -50.59) * mm});
            skLineSegment(sketch, "E32.left", {"start": v(38.59, -44.24) * mm, "end": v(38.59, -50.59) * mm});
            skLineSegment(sketch, "E32.right", {"start": v(32.24, -44.24) * mm, "end": v(32.24, -50.59) * mm});
            skLineSegment(sketch, "E33.bottom", {"start": v(-29.8, -4.57) * mm, "end": v(-36.16, -4.57) * mm});
            skLineSegment(sketch, "E33.top", {"start": v(-29.8, 1.78) * mm, "end": v(-36.16, 1.78) * mm});
            skLineSegment(sketch, "E33.left", {"start": v(-29.8, -4.57) * mm, "end": v(-29.8, 1.78) * mm});
            skLineSegment(sketch, "E33.right", {"start": v(-36.16, -4.57) * mm, "end": v(-36.16, 1.78) * mm});
            skLineSegment(sketch, "E34.bottom", {"start": v(-30.02, 25.4) * mm, "end": v(-36.37, 25.4) * mm});
            skLineSegment(sketch, "E34.top", {"start": v(-30.02, 19.05) * mm, "end": v(-36.37, 19.05) * mm});
            skLineSegment(sketch, "E34.left", {"start": v(-30.02, 25.4) * mm, "end": v(-30.02, 19.05) * mm});
            skLineSegment(sketch, "E34.right", {"start": v(-36.37, 25.4) * mm, "end": v(-36.37, 19.05) * mm});
            skLineSegment(sketch, "E35.bottom", {"start": v(-30.02, 49.79) * mm, "end": v(-36.37, 49.79) * mm});
            skLineSegment(sketch, "E35.top", {"start": v(-30.02, 43.44) * mm, "end": v(-36.37, 43.44) * mm});
            skLineSegment(sketch, "E35.left", {"start": v(-30.02, 49.79) * mm, "end": v(-30.02, 43.44) * mm});
            skLineSegment(sketch, "E35.right", {"start": v(-36.37, 49.79) * mm, "end": v(-36.37, 43.44) * mm});
            skLineSegment(sketch, "E36.bottom", {"start": v(-29.38, -21.84) * mm, "end": v(-35.73, -21.84) * mm});
            skLineSegment(sketch, "E36.top", {"start": v(-29.38, -28.2) * mm, "end": v(-35.73, -28.2) * mm});
            skLineSegment(sketch, "E36.left", {"start": v(-29.38, -21.84) * mm, "end": v(-29.38, -28.2) * mm});
            skLineSegment(sketch, "E36.right", {"start": v(-35.73, -21.84) * mm, "end": v(-35.73, -28.2) * mm});
            skLineSegment(sketch, "E37.bottom", {"start": v(-30.02, -43.94) * mm, "end": v(-36.37, -43.94) * mm});
            skLineSegment(sketch, "E37.top", {"start": v(-30.02, -50.3) * mm, "end": v(-36.37, -50.3) * mm});
            skLineSegment(sketch, "E37.left", {"start": v(-30.02, -43.94) * mm, "end": v(-30.02, -50.3) * mm});
            skLineSegment(sketch, "E37.right", {"start": v(-36.37, -43.94) * mm, "end": v(-36.37, -50.3) * mm});
            skLineSegment(sketch, "E38.bottom", {"start": v(-56.7, -4.3) * mm, "end": v(-63.06, -4.3) * mm});
            skLineSegment(sketch, "E38.top", {"start": v(-56.7, 2.05) * mm, "end": v(-63.06, 2.05) * mm});
            skLineSegment(sketch, "E38.left", {"start": v(-56.7, -4.3) * mm, "end": v(-56.7, 2.05) * mm});
            skLineSegment(sketch, "E38.right", {"start": v(-63.06, -4.3) * mm, "end": v(-63.06, 2.05) * mm});
            skLineSegment(sketch, "E39.bottom", {"start": v(-56.16, 25.68) * mm, "end": v(-62.5, 25.68) * mm});
            skLineSegment(sketch, "E39.top", {"start": v(-56.16, 19.33) * mm, "end": v(-62.5, 19.33) * mm});
            skLineSegment(sketch, "E39.left", {"start": v(-56.16, 25.68) * mm, "end": v(-56.16, 19.33) * mm});
            skLineSegment(sketch, "E39.right", {"start": v(-62.5, 25.68) * mm, "end": v(-62.5, 19.33) * mm});
            skLineSegment(sketch, "E40.bottom", {"start": v(-55.65, 48.8) * mm, "end": v(-62, 48.8) * mm});
            skLineSegment(sketch, "E40.top", {"start": v(-55.65, 42.44) * mm, "end": v(-62, 42.44) * mm});
            skLineSegment(sketch, "E40.left", {"start": v(-55.65, 48.8) * mm, "end": v(-55.65, 42.44) * mm});
            skLineSegment(sketch, "E40.right", {"start": v(-62, 48.8) * mm, "end": v(-62, 42.44) * mm});
            skLineSegment(sketch, "E41.bottom", {"start": v(-56.28, -21.57) * mm, "end": v(-62.63, -21.57) * mm});
            skLineSegment(sketch, "E41.top", {"start": v(-56.28, -27.92) * mm, "end": v(-62.63, -27.92) * mm});
            skLineSegment(sketch, "E41.left", {"start": v(-56.28, -21.57) * mm, "end": v(-56.28, -27.92) * mm});
            skLineSegment(sketch, "E41.right", {"start": v(-62.63, -21.57) * mm, "end": v(-62.63, -27.92) * mm});
            skLineSegment(sketch, "E42.bottom", {"start": v(-56.16, -44.43) * mm, "end": v(-62.5, -44.43) * mm});
            skLineSegment(sketch, "E42.top", {"start": v(-56.16, -50.78) * mm, "end": v(-62.5, -50.78) * mm});
            skLineSegment(sketch, "E42.left", {"start": v(-56.16, -44.43) * mm, "end": v(-56.16, -50.78) * mm});
            skLineSegment(sketch, "E42.right", {"start": v(-62.5, -44.43) * mm, "end": v(-62.5, -50.78) * mm});
            skLineSegment(sketch, "E43.bottom", {"start": v(62.81, -4.1) * mm, "end": v(56.46, -4.1) * mm});
            skLineSegment(sketch, "E43.top", {"start": v(62.81, 2.24) * mm, "end": v(56.46, 2.24) * mm});
            skLineSegment(sketch, "E43.left", {"start": v(62.81, -4.1) * mm, "end": v(62.81, 2.24) * mm});
            skLineSegment(sketch, "E43.right", {"start": v(56.46, -4.1) * mm, "end": v(56.46, 2.24) * mm});
            skLineSegment(sketch, "E44.bottom", {"start": v(62.6, 25.87) * mm, "end": v(56.25, 25.87) * mm});
            skLineSegment(sketch, "E44.top", {"start": v(62.6, 19.52) * mm, "end": v(56.25, 19.52) * mm});
            skLineSegment(sketch, "E44.left", {"start": v(62.6, 25.87) * mm, "end": v(62.6, 19.52) * mm});
            skLineSegment(sketch, "E44.right", {"start": v(56.25, 25.87) * mm, "end": v(56.25, 19.52) * mm});
            skLineSegment(sketch, "E45.bottom", {"start": v(62.6, 48.98) * mm, "end": v(56.25, 48.98) * mm});
            skLineSegment(sketch, "E45.top", {"start": v(62.6, 42.63) * mm, "end": v(56.25, 42.63) * mm});
            skLineSegment(sketch, "E45.left", {"start": v(62.6, 48.98) * mm, "end": v(62.6, 42.63) * mm});
            skLineSegment(sketch, "E45.right", {"start": v(56.25, 48.98) * mm, "end": v(56.25, 42.63) * mm});
            skLineSegment(sketch, "E46.bottom", {"start": v(63.24, -21.38) * mm, "end": v(56.89, -21.38) * mm});
            skLineSegment(sketch, "E46.top", {"start": v(63.24, -27.73) * mm, "end": v(56.89, -27.73) * mm});
            skLineSegment(sketch, "E46.left", {"start": v(63.24, -21.38) * mm, "end": v(63.24, -27.73) * mm});
            skLineSegment(sketch, "E46.right", {"start": v(56.89, -21.38) * mm, "end": v(56.89, -27.73) * mm});
            skLineSegment(sketch, "E47.bottom", {"start": v(62.6, -44.24) * mm, "end": v(56.25, -44.24) * mm});
            skLineSegment(sketch, "E47.top", {"start": v(62.6, -50.59) * mm, "end": v(56.25, -50.59) * mm});
            skLineSegment(sketch, "E47.left", {"start": v(62.6, -44.24) * mm, "end": v(62.6, -50.59) * mm});
            skLineSegment(sketch, "E47.right", {"start": v(56.25, -44.24) * mm, "end": v(56.25, -50.59) * mm});
            skSolve(sketch);
        }
        {
            var Q0;
            Q0 = qSketchRegion(id + "F68", true);
            extrude(context, id + "F69", {"entities" : qUnion([Q0]), "depth" : 393.7 * mm});
        }
        {
            var Q0;
            Q0 = qSketchRegion(id + "F68", true);
            extrude(context, id + "F70", {"entities" : qUnion([Q0]), "depth" : 393.7 * mm});
        }
    });
